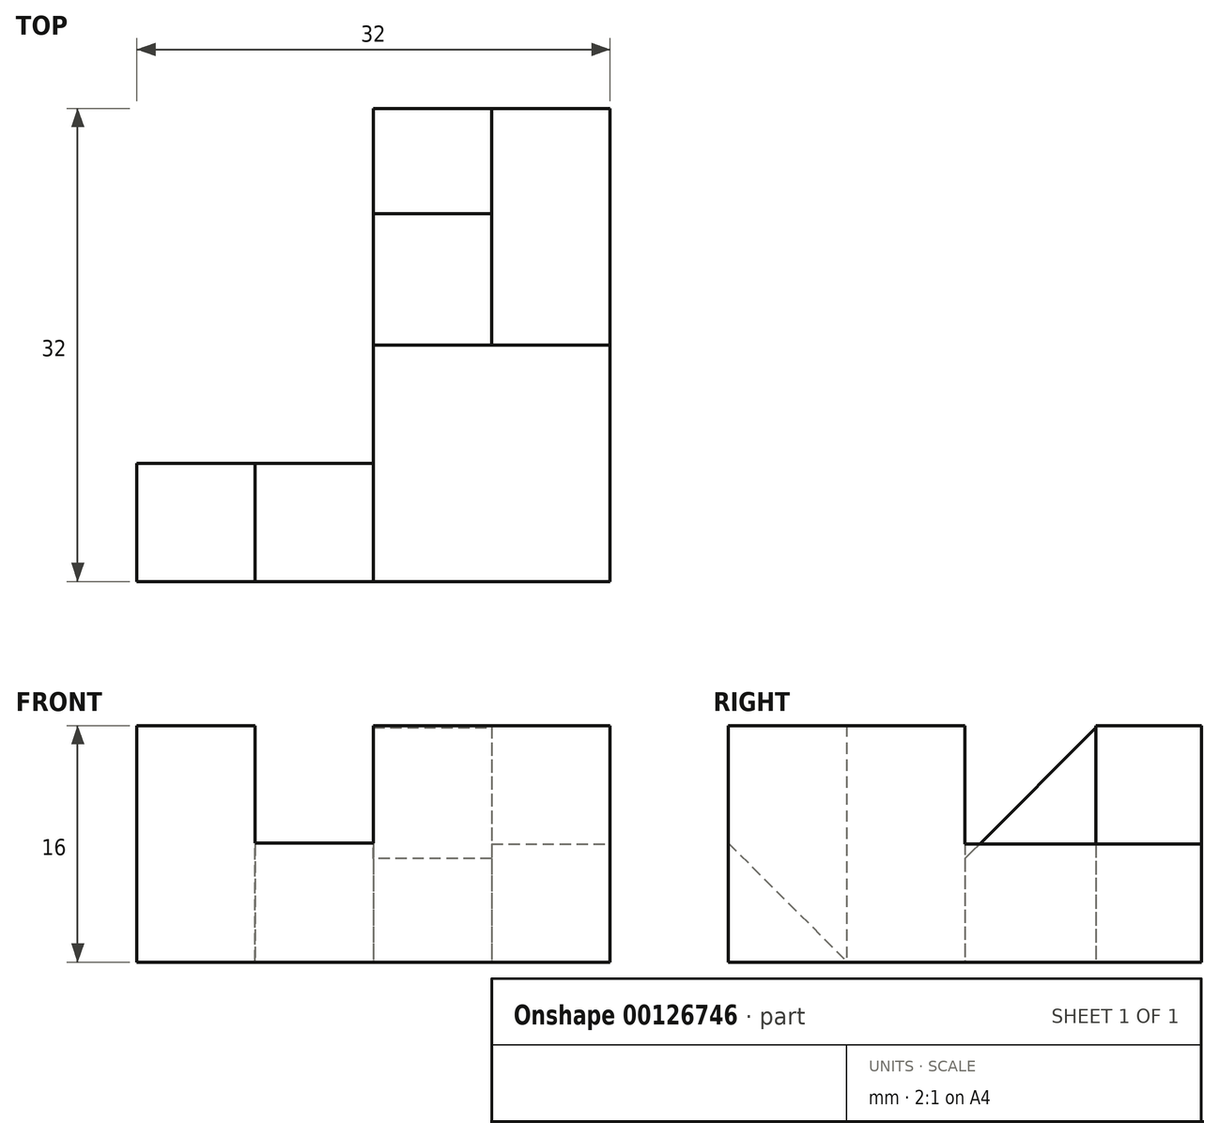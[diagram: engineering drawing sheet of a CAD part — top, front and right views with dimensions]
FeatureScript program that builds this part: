
annotation { "Feature Type Name" : "Feature", "Feature Type Description" : "" }
export const myFeature = defineFeature(function(context is Context, id is Id, definition is map)
    precondition{}
    {
        {
            var Q0;
            Q0=qCreatedBy(makeId("Top.planeOp"),FACE);
            var sketch = newSketch(context, id + "F0", { "sketchPlane" : qUnion([Q0])});
            skLineSegment(sketch, "E0", {"start": v(-31.14, 37.31) * mm, "end": v(-15.14, 37.31) * mm});
            skLineSegment(sketch, "E1", {"start": v(-15.14, 37.31) * mm, "end": v(-15.14, 5.31) * mm});
            skLineSegment(sketch, "E2", {"start": v(-15.14, 5.31) * mm, "end": v(-47.14, 5.31) * mm});
            skLineSegment(sketch, "E3", {"start": v(-47.14, 5.31) * mm, "end": v(-47.14, 13.31) * mm});
            skLineSegment(sketch, "E4", {"start": v(-47.14, 13.31) * mm, "end": v(-31.14, 13.31) * mm});
            skLineSegment(sketch, "E5", {"start": v(-31.14, 13.31) * mm, "end": v(-31.14, 37.31) * mm});
            skLineSegment(sketch, "E6", {"start": v(-39.14, 13.31) * mm, "end": v(-39.14, 5.31) * mm});
            skLineSegment(sketch, "E7", {"start": v(-31.14, 13.31) * mm, "end": v(-31.14, 5.31) * mm});
            skLineSegment(sketch, "E8", {"start": v(-31.14, 21.31) * mm, "end": v(-15.14, 21.31) * mm});
            skLineSegment(sketch, "E9", {"start": v(-23.14, 21.31) * mm, "end": v(-23.14, 37.31) * mm});
            skLineSegment(sketch, "E10", {"start": v(-31.14, 30.18) * mm, "end": v(-23.14, 30.18) * mm});
            skSolve(sketch);
        }
        {
            var Q0;
            {var subQ0=sQuery(id+"F0.wireOp",EDGE,"E6");Q0=makeQuery(id+"F0.imprint","IMPRINT",FACE,{"disambiguationData":[TD([[makeQuery(id+"F0.imprint","IMPRINT",EDGE,{"derivedFrom":subQ0}),1.0]])]});}
            extrude(context, id + "F1", {"entities" : qUnion([Q0]), "depth" : 8.05 * mm});
        }
        {
            var Q0;
            {var subQ0=sQuery(id+"F0.wireOp",EDGE,"E7");Q0=makeQuery(id+"F0.imprint","IMPRINT",FACE,{"disambiguationData":[TD([[makeQuery(id+"F0.imprint","IMPRINT",EDGE,{"derivedFrom":subQ0}),1.0]])]});}
            extrude(context, id + "F2", {"entities" : qUnion([Q0]), "operationType" : NewBodyOperationType.ADD, "depth" : 16 * mm});
        }
        {
            var Q0;
            Q0=makeQuery(id+"F1.opExtrude","CAP_EDGE",EDGE,{"disambiguationData":[OSD([sQuery(id+"F0.wireOp",EDGE,"E4")])],"isStart":false});
            chamfer(context, id + "F3", {"entities" : qUnion([Q0]), "width" : 8 * mm, "tangentPropagation" : true});
        }
        {
            var Q0;
            {var subQ0=sQuery(id+"F0.wireOp",EDGE,"E3");Q0=makeQuery(id+"F0.imprint","IMPRINT",FACE,{"disambiguationData":[TD([[makeQuery(id+"F0.imprint","IMPRINT",EDGE,{"derivedFrom":subQ0}),-1.0]])]});}
            extrude(context, id + "F4", {"entities" : qUnion([Q0]), "operationType" : NewBodyOperationType.ADD, "depth" : 16 * mm});
        }
        {
            var Q0;
            {var subQ3=sQuery(id+"F0.wireOp",EDGE,"E9");Q0=makeQuery(id+"F0.imprint","IMPRINT",FACE,{"disambiguationData":[TD([[makeQuery(id+"F0.imprint","IMPRINT",EDGE,{"derivedFrom":subQ3}),-1.0]])]});}
            extrude(context, id + "F5", {"entities" : qUnion([Q0]), "operationType" : NewBodyOperationType.ADD, "depth" : 8 * mm});
        }
        {
            var Q0;
            {var subQ5=sQuery(id+"F0.wireOp",EDGE,"E10");Q0=makeQuery(id+"F0.imprint","IMPRINT",FACE,{"disambiguationData":[TD([[makeQuery(id+"F0.imprint","IMPRINT",EDGE,{"derivedFrom":subQ5}),1.0]])]});}
            extrude(context, id + "F6", {"entities" : qUnion([Q0]), "operationType" : NewBodyOperationType.ADD, "depth" : 16 * mm});
        }
        {
            var Q0;
            {var subQ3=sQuery(id+"F0.wireOp",EDGE,"E10");Q0=makeQuery(id+"F0.imprint","IMPRINT",FACE,{"disambiguationData":[TD([[makeQuery(id+"F0.imprint","IMPRINT",EDGE,{"derivedFrom":subQ3}),-1.0]])]});}
            extrude(context, id + "F7", {"entities" : qUnion([Q0]), "depth" : 16 * mm});
        }
        {
            var Q0;
            Q0=makeQuery(id+"F7.opExtrude","CAP_EDGE",EDGE,{"disambiguationData":[OSD([sQuery(id+"F0.wireOp",EDGE,"E8")])],"isStart":false});
            chamfer(context, id + "F8", {"entities" : qUnion([Q0]), "width" : 9 * mm, "tangentPropagation" : true});
        }
    });
